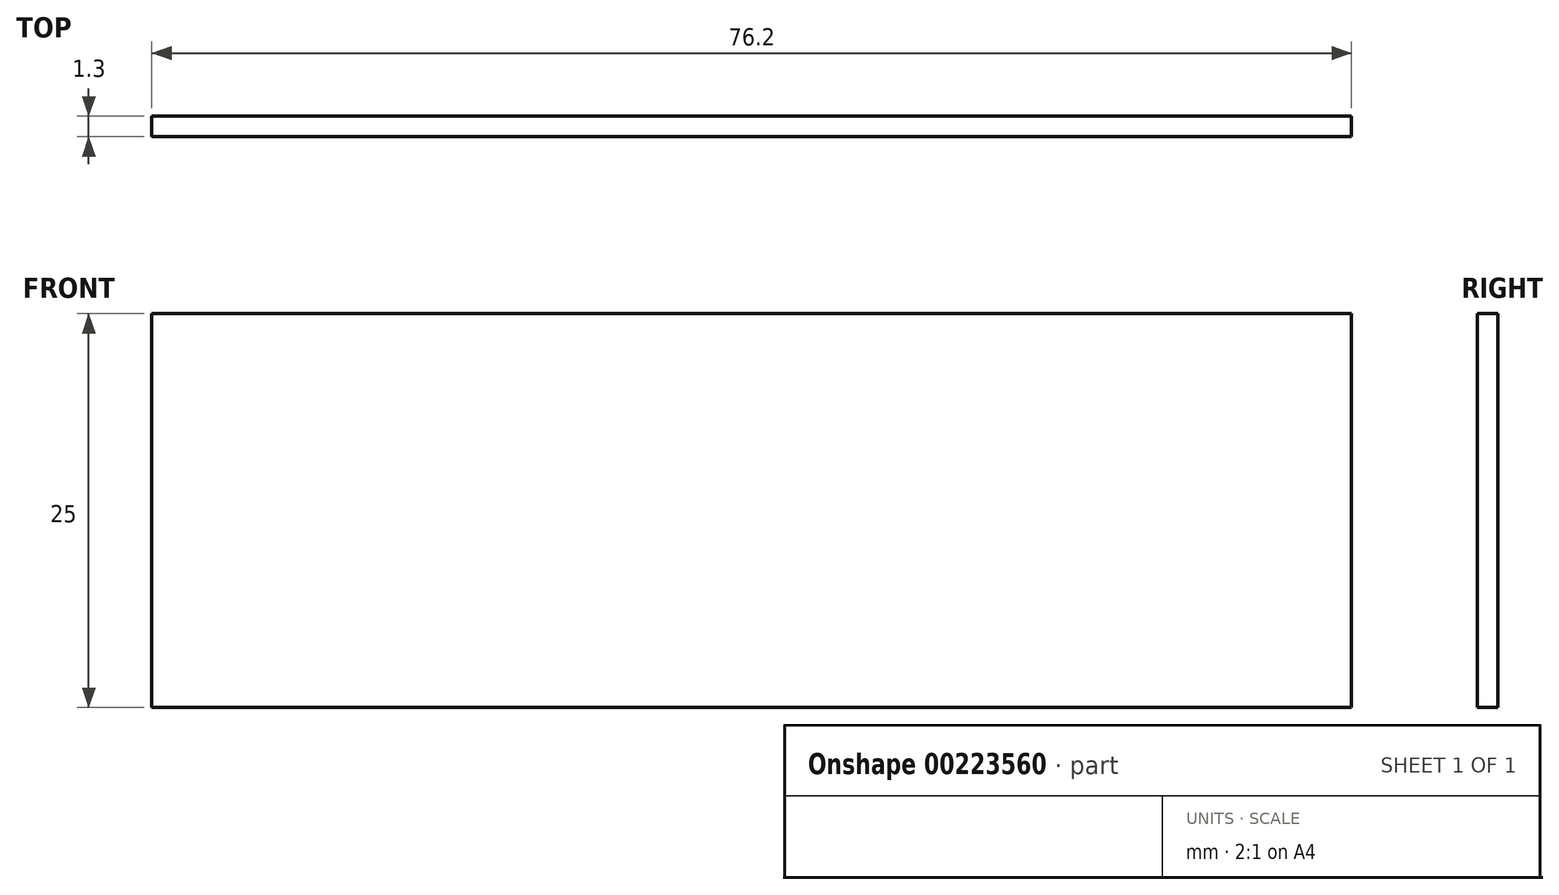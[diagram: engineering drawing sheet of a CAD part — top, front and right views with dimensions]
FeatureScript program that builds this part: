
annotation { "Feature Type Name" : "Feature", "Feature Type Description" : "" }
export const myFeature = defineFeature(function(context is Context, id is Id, definition is map)
    precondition{}
    {
        {
            var Q0;
            Q0=qCreatedBy(makeId("Front.planeOp"),FACE);
            var sketch = newSketch(context, id + "F0", { "sketchPlane" : qUnion([Q0])});
            skLineSegment(sketch, "E0.bottom", {"start": v(38.1, -12.5) * mm, "end": v(-38.1, -12.5) * mm});
            skLineSegment(sketch, "E0.top", {"start": v(38.1, 12.5) * mm, "end": v(-38.1, 12.5) * mm});
            skLineSegment(sketch, "E0.left", {"start": v(38.1, -12.5) * mm, "end": v(38.1, 12.5) * mm});
            skLineSegment(sketch, "E0.right", {"start": v(-38.1, -12.5) * mm, "end": v(-38.1, 12.5) * mm});
            skPoint(sketch, "E0.middle", {"position": v(0, 0) * mm});
            skSolve(sketch);
        }
        {
            var Q0;
            Q0=makeQuery(id+"F0.imprint","IMPRINT",FACE,{"disambiguationData":[TD([[makeQuery(id+"F0.imprint","IMPRINT",EDGE,{"derivedFrom":sQuery(id+"F0.wireOp",EDGE,"E0.bottom")}),-1.0]])]});
            extrude(context, id + "F1", {"entities" : qUnion([Q0]), "depth" : 1.3 * mm});
        }
    });
